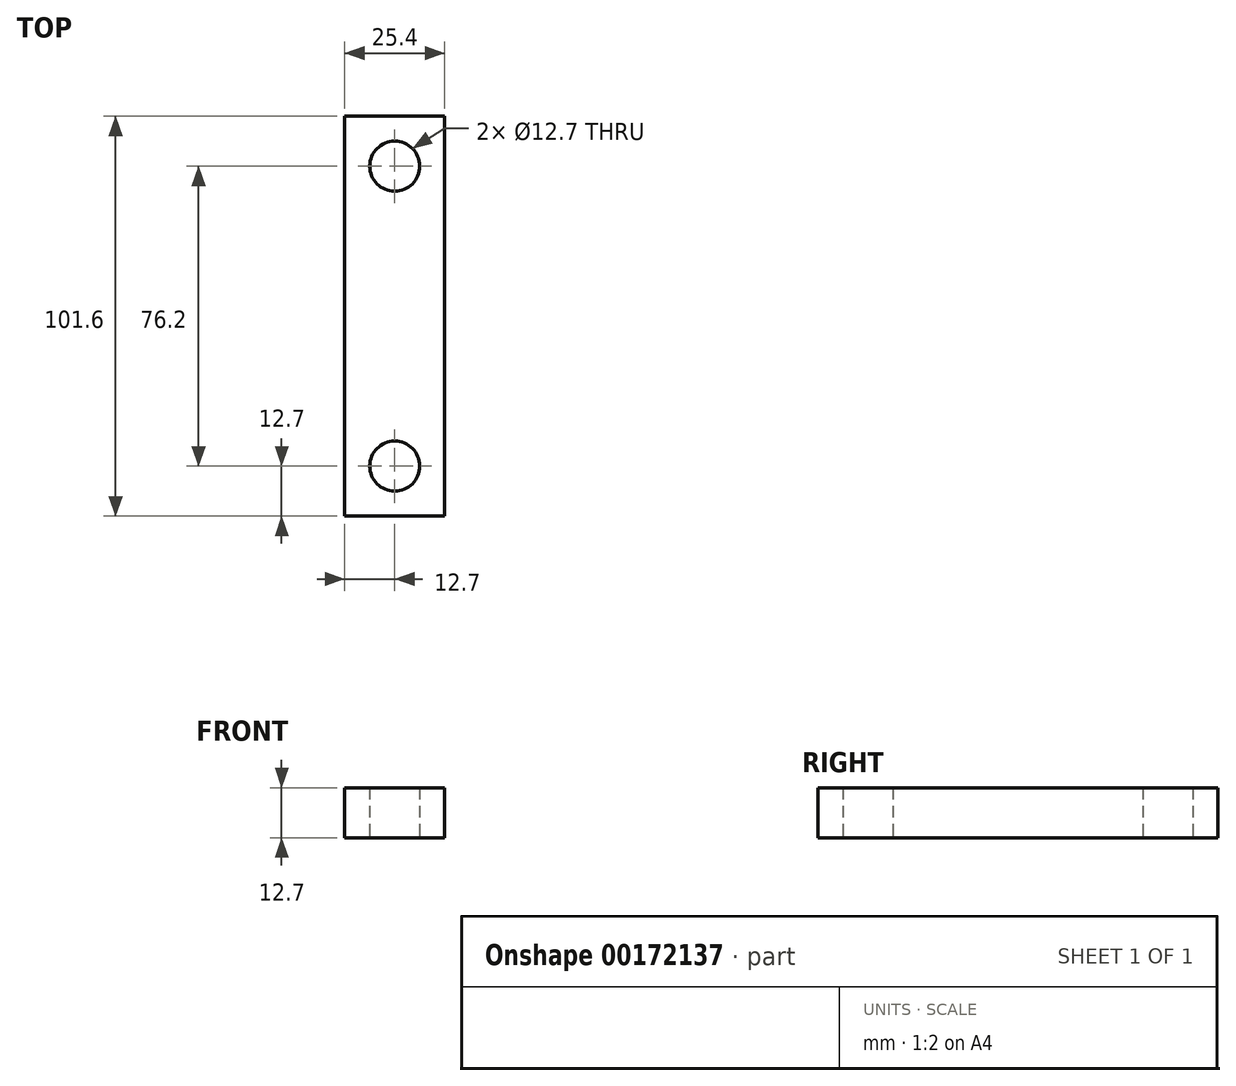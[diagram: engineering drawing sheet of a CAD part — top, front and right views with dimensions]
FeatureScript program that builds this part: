
annotation { "Feature Type Name" : "Feature", "Feature Type Description" : "" }
export const myFeature = defineFeature(function(context is Context, id is Id, definition is map)
    precondition{}
    {
        {
            var Q0;
            Q0=qCreatedBy(makeId("Top.planeOp"),FACE);
            var sketch = newSketch(context, id + "F0", { "sketchPlane" : qUnion([Q0])});
            skLineSegment(sketch, "E0.bottom", {"start": v(-12.7, 50.8) * mm, "end": v(12.7, 50.8) * mm});
            skLineSegment(sketch, "E0.top", {"start": v(-12.7, -50.8) * mm, "end": v(12.7, -50.8) * mm});
            skLineSegment(sketch, "E0.left", {"start": v(-12.7, 50.8) * mm, "end": v(-12.7, -50.8) * mm});
            skLineSegment(sketch, "E0.right", {"start": v(12.7, 50.8) * mm, "end": v(12.7, -50.8) * mm});
            skPoint(sketch, "E0.middle", {"position": v(0, 0) * mm});
            skCircle(sketch, "E1", {"center": v(0, -38.1) * mm, "radius": 6.35 * mm});
            skCircle(sketch, "E2.MirrorC", {"center": v(0, 38.1) * mm, "radius": 6.35 * mm});
            skSolve(sketch);
        }
        {
            var Q0;
            Q0=makeQuery(id+"F0.imprint","IMPRINT",FACE,{"disambiguationData":[TD([[makeQuery(id+"F0.imprint","IMPRINT",EDGE,{"derivedFrom":sQuery(id+"F0.wireOp",EDGE,"E0.bottom")}),-1.0]])]});
            extrude(context, id + "F1", {"entities" : qUnion([Q0]), "depth" : 12.7 * mm});
        }
    });
